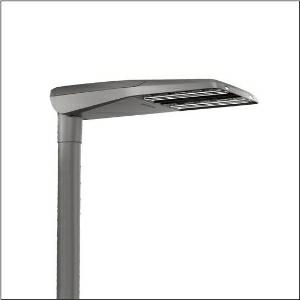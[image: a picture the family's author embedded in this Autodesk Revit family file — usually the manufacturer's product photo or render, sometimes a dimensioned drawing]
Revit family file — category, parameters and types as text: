
# Revit family: streetlight_sl_11_iq_midi___st1_0a_5xc3m41f08me_932e
name_source: partatom
category: Lighting Fixtures
units: mm (PartAtom-declared; Revit-internal decimal feet)

## family parameters
Cut with Voids When Loaded = No
Host = Face
Light Source = No
Part Type = Normal
Room Calculation Point = No
Round Connector Dimension = Use Diameter
Shared = No

## types (1)
- --- (1 x LED, 18310 lm, 124.7 W, 4000K)
    Apparent Load = 125 VA
    CIE Flux Codes = 33 66 96 100 100
    Color Rendering = 70
    Color Temperature = 4000K
    Default Elevation = 1800 mm
    Description = Streetlight SL 11 iQ midi, mast luminaire, primary light control with 3 zone facetted reflector, of plastic, silver coated, highly specular, primary optical cover: cover, of PMMA, transparent, light distribution: ST1.0a, light emission: direct distribution, primary light characteristic: asymmetric, installation type: post-top, side-entry, lamps: LED, High Power LED, rated values: 18.310lm | 124,7W | 146,8lm/W (begin service life); end service life: 18.310lm | 132,2W; at 50% lumin. flux: 9.155lm | 57,4W | 159,5lm/W, colour temperature: 4000K, colour rendering: CRI > 70, light colour: 740, light setting 1 begin service life: 100% | 18.310lm | 124,7W | 146,8lm/W | 4.000K, light setting 1 end service life: 132,2W, further light settings possible, control: optimised constant luminous flux control (CLO 2.0), Street-Remote, Desk-Remote (wireless, voltage-free reading and setting of iQ features in the workshop via application-optimized NFC function/RFID function), Light-Fading, Smart-Wire, Night-Set, Lumen-Switch, Temp-Guard, Auto-Match, with cable H07RN-F 5x 1.5mm², mains connection: 230..240V, AC, 50/60Hz, connection cable pre-assembled, cable length: 12,5m, luminaire housing, of diecast aluminium, powder-coated, Siteco® metallic grey (DB 702S), please order mast flange separately, inclination adjustable without tools: 0°, 5°, 10°, 15° (post-top) | 0°, -5°, -10°, -15° (side-entry), sealing non-destructively replaceable, multi-level sealing system, length: 780mm, width: 376mm, height: 118mm, mast flange for spigot size: 42mm (side-entry): 5XC10008XM4, 60/48mm (side-entry/post-top): 5XC10108XM2, 76/60mm (side-entry/post-top): 5XC10108XM1, equipment: Power, protection rating (complete): IP66, insulation class (complete): insulation class II (safety insulation), certification: CE, ENEC, ENEC+, VDE, impact resistance: IK10, permissible operating ambient temperature for outdoor applications: -25..+50°C, standard-compliant lighting for roads and squares, Environmental Product Declaration (EPD) tested and certified by an independent institute, packaging unit: 1 piece

Light Distribution: ST1.0a
    Height = 118 mm
    Lamp = 1 x LED
    Lamp Light Flux = 18310 lm
    Lamp Power = 124.7 W
    Lamp count = 1
    Length = 780 mm
    Luminous efficacy = 147 lm/W
    Manufacturer = Siteco
    ModVariant = No
    Model = 5XC3M41F08ME
    Number of Poles = 1
    OnlyDefault = Yes
    Power Factor = 1
    Product Name = Streetlight SL 11 iQ midi | ST1.0a
    Product group = mast luminaire | pylon top
    ProductGroupID = 6100
    Protection Class = Protection class II
    Protection Degree = IP 66
    RLX_Detail_Level = 1
    RLX_Emergency_Light_Flux = 0 lm
    RLX_Emergency_Type = 0
    RLX_Emergency_Type_DB = No
    RlxData = <blob elided: 70505 chars, md5=0268909f>
    Socket = socket
    Standby Power = 0 W
    System Light Flux = 18310 lm
    System Power = 125 W
    Type Comments = factory setting: luminous flux: 100 % | dim-lin: 254 | 557 mA
    Type Image = l_1005960.jpg
    URL = http://relux.com
    VarID = @adj_110083
    Voltage = 0 V
    Weight = 0.00 kg
    Width = 376 mm

## geometry (parser evidence)
native form markers: Blend x4, Sweep x11
no freeform markers — native parametric forms only
